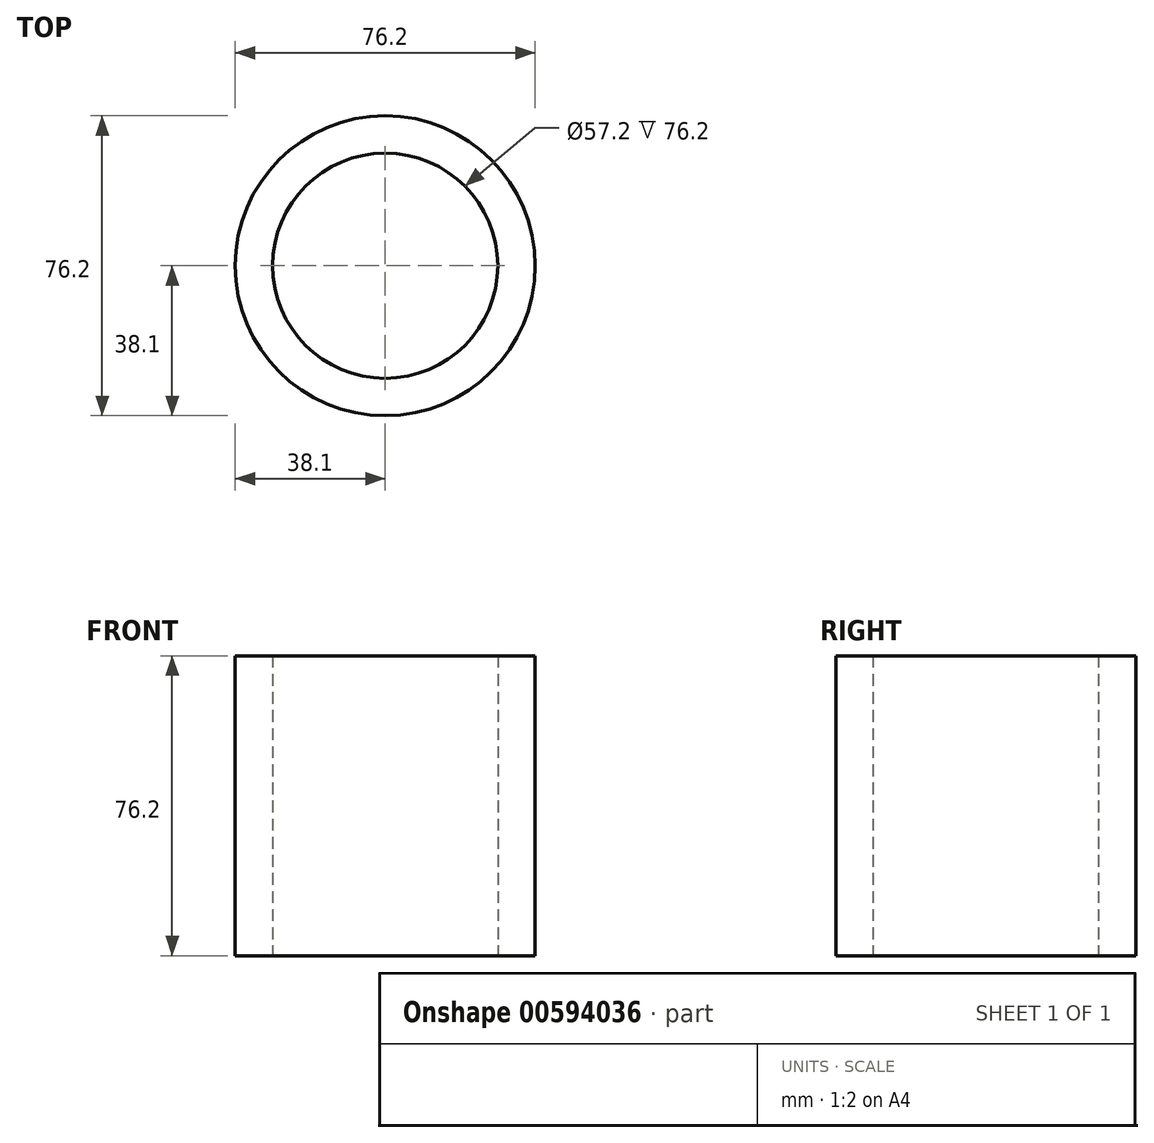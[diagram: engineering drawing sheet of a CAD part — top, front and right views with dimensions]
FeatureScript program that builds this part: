
annotation { "Feature Type Name" : "Feature", "Feature Type Description" : "" }
export const myFeature = defineFeature(function(context is Context, id is Id, definition is map)
    precondition{}
    {
        {
            var Q0;
            Q0=qCreatedBy(makeId("Top.planeOp"),FACE);
            var sketch = newSketch(context, id + "F0", { "sketchPlane" : qUnion([Q0])});
            skCircle(sketch, "E0", {"center": v(0, 0) * mm, "radius": 38.1 * mm});
            skCircle(sketch, "E1", {"center": v(0, 0) * mm, "radius": 28.6 * mm});
            skSolve(sketch);
        }
        {
            var Q0;
            Q0=makeQuery(id+"F0.imprint","IMPRINT",FACE,{"disambiguationData":[TD([[makeQuery(id+"F0.imprint","IMPRINT",EDGE,{"derivedFrom":sQuery(id+"F0.wireOp",EDGE,"E0")}),1.0]])]});
            extrude(context, id + "F1", {"entities" : qUnion([Q0]), "depth" : 76.2 * mm, "offsetDistance" : 25.4 * mm});
        }
    });
